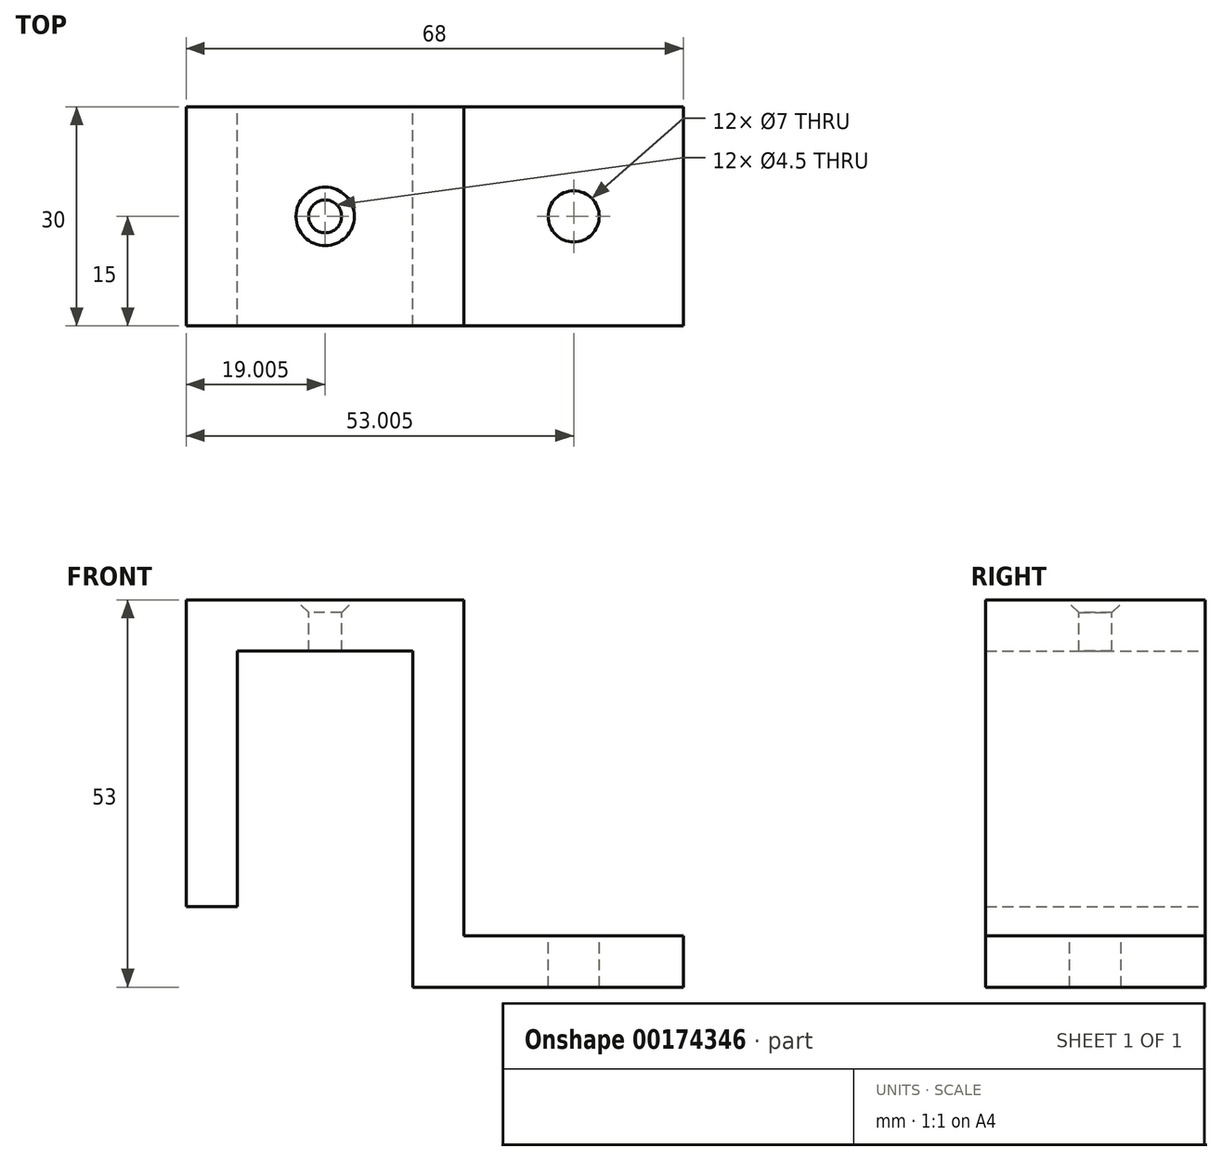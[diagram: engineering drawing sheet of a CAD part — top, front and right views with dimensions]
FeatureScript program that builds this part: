
annotation { "Feature Type Name" : "Feature", "Feature Type Description" : "" }
export const myFeature = defineFeature(function(context is Context, id is Id, definition is map)
    precondition{}
    {
        {
            var Q0;
            Q0=qCreatedBy(makeId("Front.planeOp"),FACE);
            var sketch = newSketch(context, id + "F0", { "sketchPlane" : qUnion([Q0])});
            skLineSegment(sketch, "E0", {"start": v(-48.3, 15.03) * mm, "end": v(-48.3, 50.03) * mm});
            skLineSegment(sketch, "E1", {"start": v(-48.3, 50.03) * mm, "end": v(-24.3, 50.03) * mm});
            skLineSegment(sketch, "E2", {"start": v(-24.3, 50.03) * mm, "end": v(-24.3, 4.03) * mm});
            skLineSegment(sketch, "E3", {"start": v(-24.3, 4.03) * mm, "end": v(12.7, 4.03) * mm});
            skLineSegment(sketch, "E4", {"start": v(12.7, 4.03) * mm, "end": v(12.7, 11.03) * mm});
            skLineSegment(sketch, "E5", {"start": v(12.7, 11.03) * mm, "end": v(-17.3, 11.03) * mm});
            skLineSegment(sketch, "E6", {"start": v(-17.3, 11.03) * mm, "end": v(-17.3, 57.03) * mm});
            skLineSegment(sketch, "E7", {"start": v(-17.3, 57.03) * mm, "end": v(-55.3, 57.03) * mm});
            skLineSegment(sketch, "E8", {"start": v(-55.3, 57.03) * mm, "end": v(-55.3, 15.03) * mm});
            skLineSegment(sketch, "E9", {"start": v(-55.3, 15.03) * mm, "end": v(-48.3, 15.03) * mm});
            skSolve(sketch);
        }
        {
            var Q0;
            Q0=makeQuery(id+"F0.imprint","IMPRINT",FACE,{"disambiguationData":[TD([[makeQuery(id+"F0.imprint","IMPRINT",EDGE,{"derivedFrom":sQuery(id+"F0.wireOp",EDGE,"E0")}),1.0]])]});
            extrude(context, id + "F1", {"entities" : qUnion([Q0]), "endBound" : BoundingType.SYMMETRIC, "depth" : 30 * mm});
        }
        {
            var Q0;
            Q0=makeQuery(id+"F1.opExtrude","SWEPT_FACE",FACE,{"disambiguationData":[OSD([sQuery(id+"F0.wireOp",EDGE,"E5")])]});
            var sketch = newSketch(context, id + "F2", { "sketchPlane" : qUnion([Q0])});
            skPoint(sketch, "E10", {"position": v(-2.3, 0) * mm});
            skSolve(sketch);
        }
        {
            var Q0;
            Q0=sQuery(id+"F2.wireOp",VERTEX,"E10");
            var Q1;
            Q1=makeQuery(id+"F1.opExtrude","SWEPT_BODY",BODY,{"disambiguationData":[OSD([sQuery(id+"F0.wireOp",EDGE,"E0"),sQuery(id+"F0.wireOp",EDGE,"E1"),sQuery(id+"F0.wireOp",EDGE,"E2"),sQuery(id+"F0.wireOp",EDGE,"E3"),sQuery(id+"F0.wireOp",EDGE,"E4"),sQuery(id+"F0.wireOp",EDGE,"E5"),sQuery(id+"F0.wireOp",EDGE,"E6"),sQuery(id+"F0.wireOp",EDGE,"E7"),sQuery(id+"F0.wireOp",EDGE,"E8"),sQuery(id+"F0.wireOp",EDGE,"E9")])]});
            hole(context, id + "F3", {"style" : HoleStyle.SIMPLE, "endStyle" : HoleEndStyle.THROUGH, "holeDiameter" : 7 * mm, "startFromSketch" : true, "locations" : qUnion([Q0]), "scope" : qUnion([Q1]), "isTappedThrough" : true});
        }
        {
            var Q0;
            Q0=makeQuery(id+"F1.opExtrude","SWEPT_FACE",FACE,{"disambiguationData":[OSD([sQuery(id+"F0.wireOp",EDGE,"E7")])]});
            var sketch = newSketch(context, id + "F4", { "sketchPlane" : qUnion([Q0])});
            skPoint(sketch, "E11", {"position": v(-36.3, 0) * mm});
            skSolve(sketch);
        }
        {
            var Q0;
            Q0=sQuery(id+"F4.wireOp",VERTEX,"E11");
            var Q1;
            Q1=makeQuery(id+"F1.opExtrude","SWEPT_BODY",BODY,{"disambiguationData":[OSD([sQuery(id+"F0.wireOp",EDGE,"E0"),sQuery(id+"F0.wireOp",EDGE,"E1"),sQuery(id+"F0.wireOp",EDGE,"E2"),sQuery(id+"F0.wireOp",EDGE,"E3"),sQuery(id+"F0.wireOp",EDGE,"E4"),sQuery(id+"F0.wireOp",EDGE,"E5"),sQuery(id+"F0.wireOp",EDGE,"E6"),sQuery(id+"F0.wireOp",EDGE,"E7"),sQuery(id+"F0.wireOp",EDGE,"E8"),sQuery(id+"F0.wireOp",EDGE,"E9")])]});
            hole(context, id + "F5", {"style" : HoleStyle.C_SINK, "endStyle" : HoleEndStyle.THROUGH, "holeDiameter" : 4.5 * mm, "cSinkDiameter" : 8 * mm, "cSinkAngle" : 90 * degree, "startFromSketch" : true, "locations" : qUnion([Q0]), "scope" : qUnion([Q1]), "isTappedThrough" : true});
        }
    });
